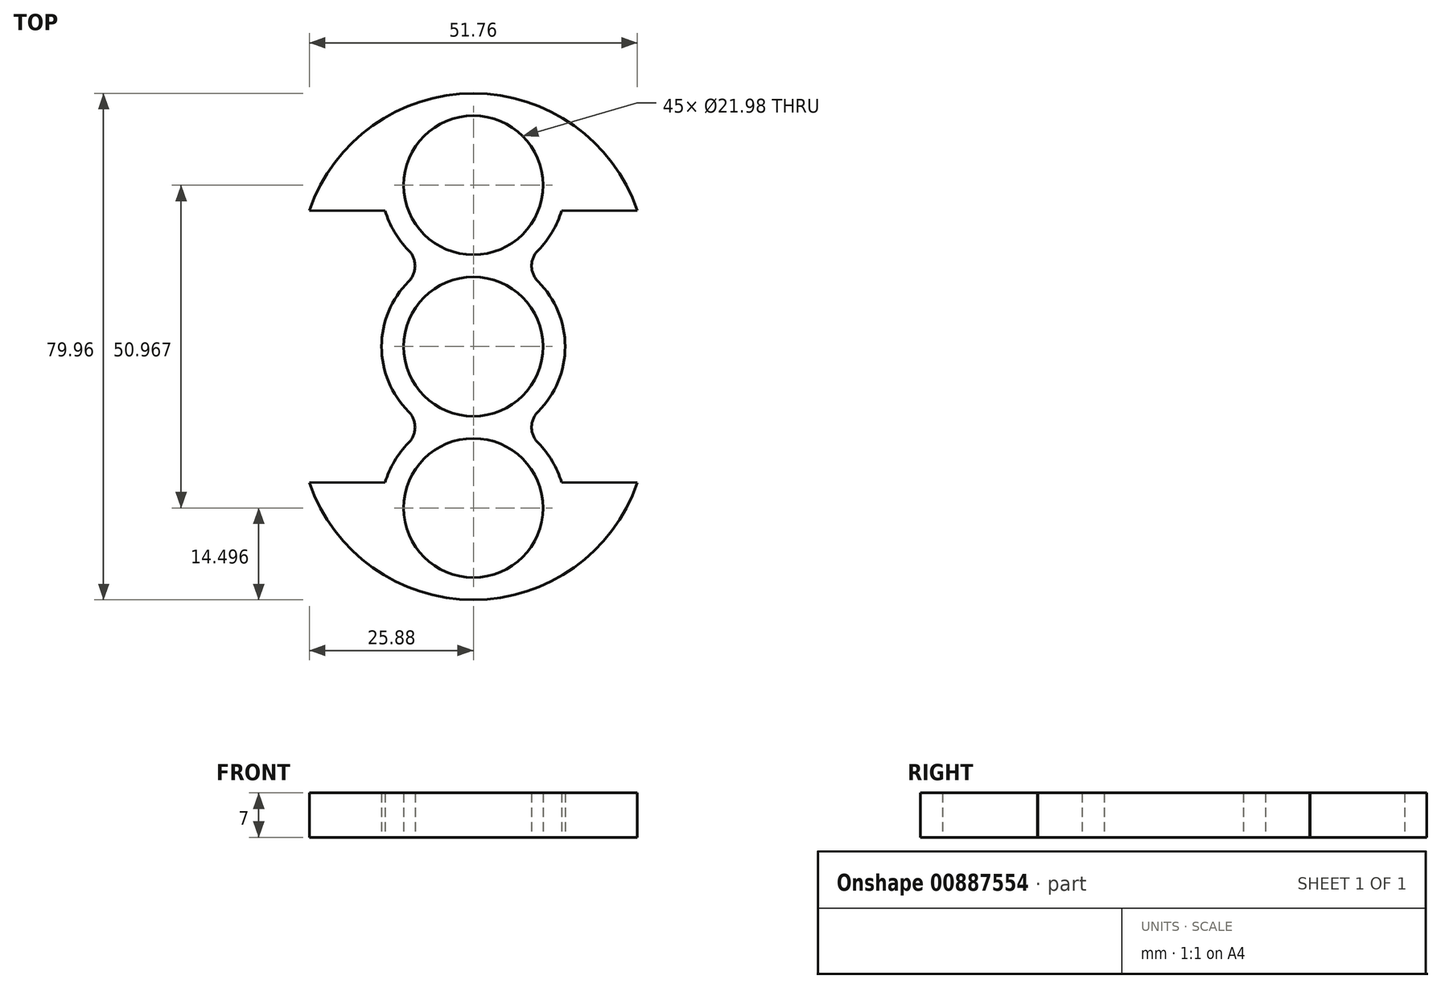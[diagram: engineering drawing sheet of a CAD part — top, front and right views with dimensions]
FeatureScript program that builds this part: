
annotation { "Feature Type Name" : "Feature", "Feature Type Description" : "" }
export const myFeature = defineFeature(function(context is Context, id is Id, definition is map)
    precondition{}
    {
        {
            var Q0;
            Q0=qCreatedBy(makeId("Top.planeOp"),FACE);
            var sketch = newSketch(context, id + "F0", { "sketchPlane" : qUnion([Q0])});
            skCircle(sketch, "E0", {"center": v(0, 0) * mm, "radius": 11 * mm});
            skCircle(sketch, "E1", {"center": v(0, 25.48) * mm, "radius": 11 * mm});
            skCircle(sketch, "E2", {"center": v(0, -25.48) * mm, "radius": 11 * mm});
            skLineSegment(sketch, "E3", {"start": v(0, 25.48) * mm, "end": v(0, -25.48) * mm, "construction": true});
            skLineSegment(sketch, "E4.bottom", {"start": v(-29.85, 57.15) * mm, "end": v(29.85, 57.15) * mm, "construction": true});
            skLineSegment(sketch, "E4.top", {"start": v(-29.85, -57.15) * mm, "end": v(29.85, -57.15) * mm, "construction": true});
            skLineSegment(sketch, "E4.left", {"start": v(-29.84, 57.15) * mm, "end": v(-29.85, -57.15) * mm, "construction": true});
            skLineSegment(sketch, "E4.right", {"start": v(29.85, 57.15) * mm, "end": v(29.84, -57.15) * mm, "construction": true});
            skPoint(sketch, "E5", {"position": v(0, 57.15) * mm});
            skPoint(sketch, "E6", {"position": v(-29.85, 0) * mm});
            skSolve(sketch);
        }
        {
            var Q0;
            Q0=qCreatedBy(makeId("Top.planeOp"),FACE);
            var sketch = newSketch(context, id + "F1", { "sketchPlane" : qUnion([Q0])});
            skCircle(sketch, "E7", {"center": v(0, 25.48) * mm, "radius": 11 * mm});
            skCircle(sketch, "E8", {"center": v(0, 0) * mm, "radius": 11 * mm});
            skCircle(sketch, "E9", {"center": v(0, -25.48) * mm, "radius": 11 * mm});
            skLineSegment(sketch, "E10.bottom", {"start": v(-29.85, 57.15) * mm, "end": v(29.84, 57.15) * mm, "construction": true});
            skLineSegment(sketch, "E10.top", {"start": v(-29.85, -57.15) * mm, "end": v(29.84, -57.15) * mm, "construction": true});
            skLineSegment(sketch, "E10.left", {"start": v(-29.85, 57.15) * mm, "end": v(-29.85, -57.15) * mm, "construction": true});
            skLineSegment(sketch, "E10.right", {"start": v(29.85, 57.15) * mm, "end": v(29.85, -57.15) * mm, "construction": true});
            skPoint(sketch, "E11", {"position": v(-29.85, 0) * mm});
            skPoint(sketch, "E12", {"position": v(0, 57.15) * mm});
            skArc(sketch, "E13.0", {"start": v(10.23, 15.22) * mm, "mid": v(0, 39.98) * mm, "end": v(-10.23, 15.22) * mm});
            skArc(sketch, "E14.0", {"start": v(-10.23, 10.26) * mm, "mid": v(-14.5, 0) * mm, "end": v(-10.23, -10.26) * mm});
            skArc(sketch, "E15.0", {"start": v(-10.23, -15.22) * mm, "mid": v(0, -39.98) * mm, "end": v(10.23, -15.22) * mm});
            skArc(sketch, "E16.trimOffspring", {"start": v(10.23, -10.26) * mm, "mid": v(14.5, 0) * mm, "end": v(10.23, 10.26) * mm});
            skPoint(sketch, "E17.visualSharp", {"position": v(-6.9, 12.74) * mm});
            skArc(sketch, "E17.filletArc", {"start": v(-10.23, 10.26) * mm, "mid": v(-9.2, 12.74) * mm, "end": v(-10.23, 15.22) * mm});
            skPoint(sketch, "E18.visualSharp", {"position": v(6.9, 12.74) * mm});
            skArc(sketch, "E18.filletArc", {"start": v(10.23, 15.22) * mm, "mid": v(9.2, 12.74) * mm, "end": v(10.23, 10.26) * mm});
            skPoint(sketch, "E19.visualSharp", {"position": v(6.9, -12.74) * mm});
            skArc(sketch, "E19.filletArc", {"start": v(10.23, -10.26) * mm, "mid": v(9.2, -12.74) * mm, "end": v(10.23, -15.22) * mm});
            skPoint(sketch, "E20.visualSharp", {"position": v(-6.9, -12.74) * mm});
            skArc(sketch, "E20.filletArc", {"start": v(-10.23, -15.22) * mm, "mid": v(-9.2, -12.74) * mm, "end": v(-10.23, -10.26) * mm});
            skPoint(sketch, "E21.end.orphan", {"position": v(10.23, 35.75) * mm});
            skArc(sketch, "E22", {"start": v(25.88, 21.52) * mm, "mid": v(15.9, 34.89) * mm, "end": v(0, 39.98) * mm});
            skLineSegment(sketch, "E23", {"start": v(25.88, 21.52) * mm, "end": v(13.92, 21.46) * mm});
            skLineSegment(sketch, "E24", {"start": v(0, 0) * mm, "end": v(23.42, 0) * mm, "construction": true});
            skLineSegment(sketch, "E25", {"start": v(23.42, 0) * mm, "end": v(0, 0) * mm});
            skLineSegment(sketch, "E26", {"start": v(0, 0) * mm, "end": v(0, -19.43) * mm, "construction": true});
            skLineSegment(sketch, "E27.MirrorCS", {"start": v(25.88, -21.52) * mm, "end": v(13.92, -21.46) * mm});
            skArc(sketch, "E28.MirrorCS", {"start": v(25.88, -21.52) * mm, "mid": v(15.9, -34.89) * mm, "end": v(0, -39.98) * mm});
            skLineSegment(sketch, "E29.MirrorCS", {"start": v(-25.88, -21.52) * mm, "end": v(-13.92, -21.46) * mm});
            skArc(sketch, "E30.MirrorCS", {"start": v(-25.88, -21.52) * mm, "mid": v(-15.9, -34.89) * mm, "end": v(0, -39.98) * mm});
            skLineSegment(sketch, "E31.MirrorCS", {"start": v(-25.88, 21.52) * mm, "end": v(-13.92, 21.46) * mm});
            skArc(sketch, "E32.MirrorCS", {"start": v(-25.88, 21.52) * mm, "mid": v(-15.9, 34.89) * mm, "end": v(0, 39.98) * mm});
            skSolve(sketch);
        }
        {
            var Q0;
            Q0 = qSketchRegion(id + "F1", true);
            extrude(context, id + "F2", {"entities" : qUnion([Q0]), "depth" : 7 * mm, "offsetDistance" : 25.4 * mm});
        }
    });
